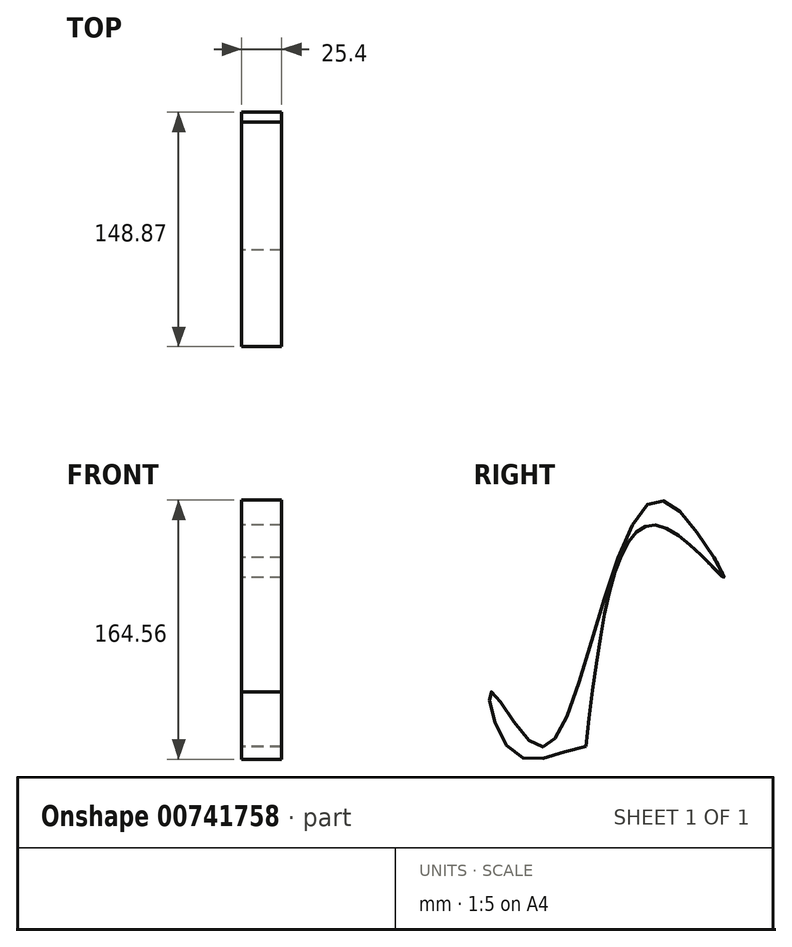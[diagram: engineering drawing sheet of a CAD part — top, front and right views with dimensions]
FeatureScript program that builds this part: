
annotation { "Feature Type Name" : "Feature", "Feature Type Description" : "" }
export const myFeature = defineFeature(function(context is Context, id is Id, definition is map)
    precondition{}
    {
        {
            var Q0;
            Q0=qCreatedBy(makeId("Right.planeOp"),FACE);
            var sketch = newSketch(context, id + "F0", { "sketchPlane" : qUnion([Q0])});
            skFitSpline(sketch, "E0", {"points": [v(75.44, 38.23) * mm, v(35.36, 73.33) * mm, v(-18.72, -64.33) * mm, v(-39.72, -79.94) * mm, v(-66.4, -47.01) * mm, v(-51.53, -86.09) * mm, v(-6, -81.74) * mm], "startDerivative": vector(-248.97, 380.64) * mm, "endDerivative": vector(306.23, 47.9) * mm});
            skFitSpline(sketch, "E1", {"points": [v(-6, -81.74) * mm, v(38.39, 58.76) * mm, v(81.28, 25.77) * mm, v(75.44, 38.23) * mm], "startDerivative": vector(49.14, 412.46) * mm, "endDerivative": vector(-68.96, 123.07) * mm});
            skSolve(sketch);
        }
        {
            var Q0;
            Q0=makeQuery(id+"F0.imprint","IMPRINT",FACE,{"disambiguationData":[TD([[makeQuery(id+"F0.imprint","IMPRINT",EDGE,{"derivedFrom":sQuery(id+"F0.wireOp",EDGE,"E0")}),1.0]])]});
            extrude(context, id + "F1", {"entities" : qUnion([Q0]), "depth" : 25.4 * mm, "offsetDistance" : 25.4 * mm});
        }
    });
